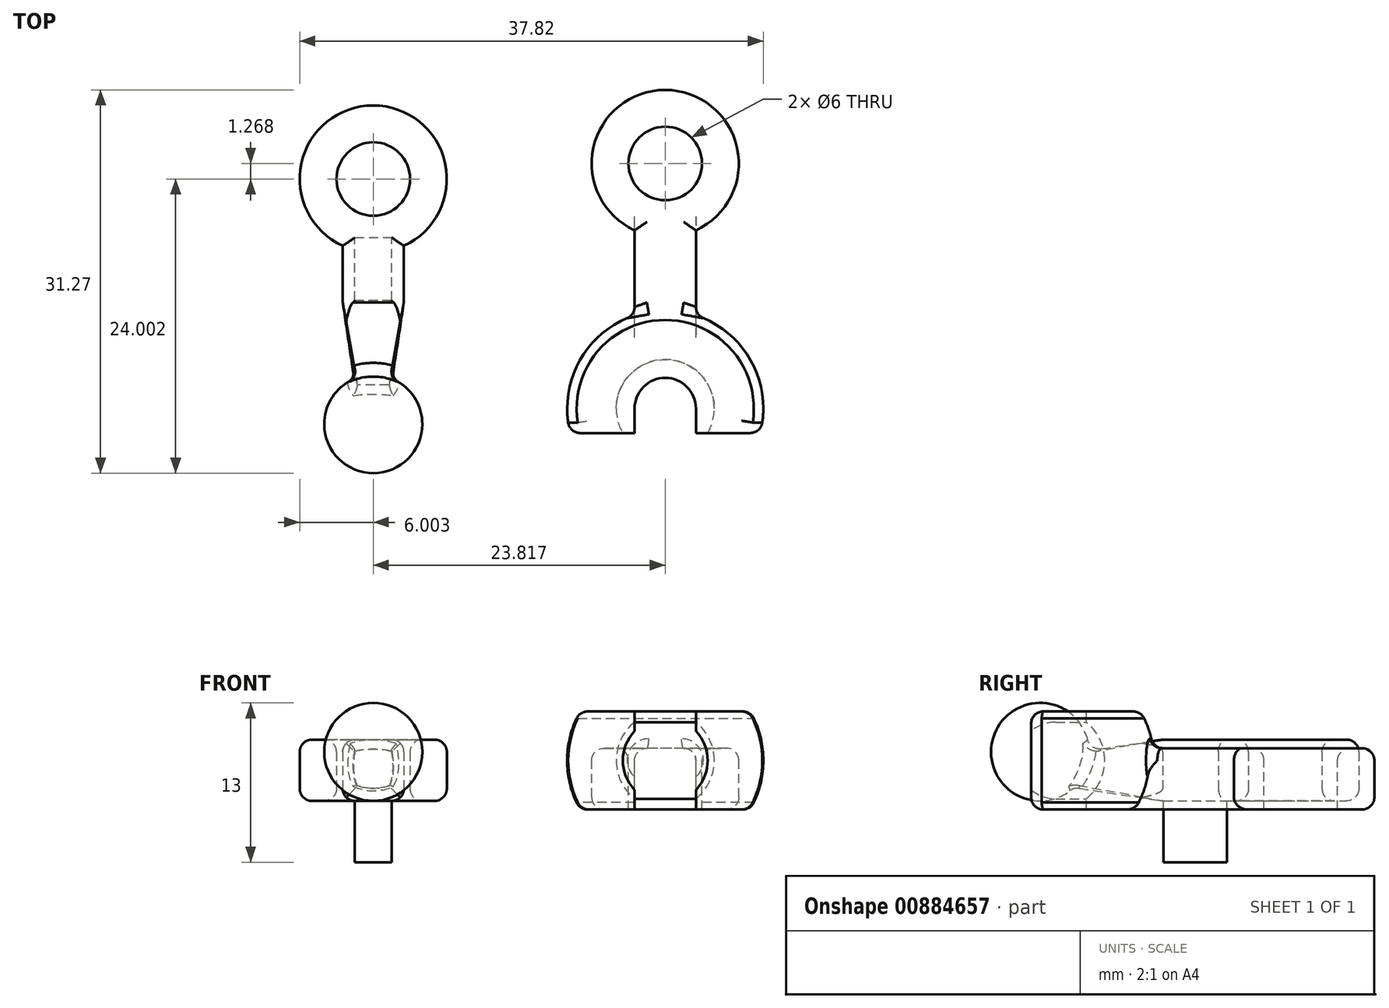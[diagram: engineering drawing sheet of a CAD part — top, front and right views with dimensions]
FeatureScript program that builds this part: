
annotation { "Feature Type Name" : "Feature", "Feature Type Description" : "" }
export const myFeature = defineFeature(function(context is Context, id is Id, definition is map)
    precondition{}
    {
        {
            var Q0;
            Q0=qCreatedBy(makeId("Front.planeOp"),FACE);
            var sketch = newSketch(context, id + "F0", { "sketchPlane" : qUnion([Q0])});
            skLineSegment(sketch, "E0.bottom", {"start": v(0, 0) * mm, "end": v(5, 0) * mm});
            skLineSegment(sketch, "E0.top", {"start": v(0, -5) * mm, "end": v(5, -5) * mm});
            skLineSegment(sketch, "E0.left", {"start": v(0, 0) * mm, "end": v(0, -5) * mm});
            skLineSegment(sketch, "E0.right", {"start": v(5, 0) * mm, "end": v(5, -5) * mm});
            skSolve(sketch);
        }
        {
            var Q0;
            Q0=makeQuery(id+"F0.imprint","IMPRINT",FACE,{"disambiguationData":[TD([[makeQuery(id+"F0.imprint","IMPRINT",EDGE,{"derivedFrom":sQuery(id+"F0.wireOp",EDGE,"E0.bottom")}),-1.0]])]});
            extrude(context, id + "F1", {"entities" : qUnion([Q0]), "depth" : 20 * mm, "offsetDistance" : 25 * mm});
        }
        {
            var Q0;
            Q0=makeQuery(id+"F1.opExtrude","CAP_FACE",FACE,{"disambiguationData":[OSD([sQuery(id+"F0.wireOp",EDGE,"E0.bottom"),sQuery(id+"F0.wireOp",EDGE,"E0.top"),sQuery(id+"F0.wireOp",EDGE,"E0.left"),sQuery(id+"F0.wireOp",EDGE,"E0.right")])],"isStart":false});
            var sketch = newSketch(context, id + "F2", { "sketchPlane" : qUnion([Q0])});
            skLineSegment(sketch, "E1", {"start": v(2.5, -1) * mm, "end": v(2.5, -9) * mm, "construction": true});
            skLineSegment(sketch, "E2.0", {"start": v(0, 0) * mm, "end": v(2.5, 0) * mm});
            skLineSegment(sketch, "E3", {"start": v(2.5, 0) * mm, "end": v(5, 0) * mm});
            skLineSegment(sketch, "E4", {"start": v(-5.5, -1) * mm, "end": v(-5.5, -1) * mm});
            skLineSegment(sketch, "E5", {"start": v(-5.5, -1) * mm, "end": v(10.5, -1) * mm});
            skArc(sketch, "E6", {"start": v(10.5, -1) * mm, "mid": v(2.5, 7) * mm, "end": v(-5.5, -1) * mm});
            skArc(sketch, "E7", {"start": v(-5.5, -1) * mm, "mid": v(2.5, -9) * mm, "end": v(10.5, -1) * mm, "construction": true});
            skSolve(sketch);
        }
        {
            var Q0;
            {var subQ7=sQuery(id+"F2.wireOp",EDGE,"E2.0");Q0=makeQuery(id+"F2.imprint","IMPRINT",FACE,{"disambiguationData":[TD([[makeQuery(id+"F2.imprint","IMPRINT",EDGE,{"derivedFrom":subQ7}),1.0]])]});}
            var Q1;
            Q1=sQuery(id+"F2.wireOp",EDGE,"E5");
            revolve(context, id + "F3", {"operationType" : NewBodyOperationType.ADD, "surfaceOperationType" : NewSurfaceOperationType.NEW, "entities" : qUnion([Q0]), "axis" : qUnion([Q1]), "revolveType" : RevolveType.FULL});
        }
        {
            var Q0;
            Q0=makeQuery(id+"F1.opExtrude","SWEPT_FACE",FACE,{"disambiguationData":[OSD([sQuery(id+"F0.wireOp",EDGE,"E0.bottom")])]});
            cPlane(context, id + "F4", {"entities" : qUnion([Q0]), "cplaneType" : CPlaneType.OFFSET, "offset" : 7 * mm, "width" : 150 * mm, "height" : 150 * mm});
        }
        {
            var Q0;
            Q0=makeQuery(id+"F1.opExtrude","SWEPT_FACE",FACE,{"disambiguationData":[OSD([sQuery(id+"F0.wireOp",EDGE,"E0.top")])]});
            cPlane(context, id + "F5", {"entities" : qUnion([Q0]), "cplaneType" : CPlaneType.OFFSET, "offset" : 4 * mm, "width" : 150 * mm, "height" : 150 * mm});
        }
        {
            var Q0;
            Q0=makeQuery(id+"F1.opExtrude","CAP_FACE",FACE,{"disambiguationData":[OSD([sQuery(id+"F0.wireOp",EDGE,"E0.bottom"),sQuery(id+"F0.wireOp",EDGE,"E0.top"),sQuery(id+"F0.wireOp",EDGE,"E0.left"),sQuery(id+"F0.wireOp",EDGE,"E0.right")])],"isStart":true});
            cPlane(context, id + "F6", {"entities" : qUnion([Q0]), "cplaneType" : CPlaneType.OFFSET, "offset" : 28 * mm, "oppositeDirection" : true, "width" : 150 * mm, "height" : 150 * mm});
        }
        {
            var Q0;
            Q0=qCreatedBy(id+"F4.planeOp",FACE);
            var sketch = newSketch(context, id + "F7", { "sketchPlane" : qUnion([Q0])});
            skLineSegment(sketch, "E8.bottom", {"start": v(-14.83, -1.3) * mm, "end": v(22.96, -1.3) * mm});
            skLineSegment(sketch, "E8.top", {"start": v(-14.83, -38.22) * mm, "end": v(22.96, -38.22) * mm});
            skLineSegment(sketch, "E8.left", {"start": v(-14.83, -1.3) * mm, "end": v(-14.83, -38.22) * mm});
            skLineSegment(sketch, "E8.right", {"start": v(22.96, -1.3) * mm, "end": v(22.96, -38.22) * mm});
            skSolve(sketch);
        }
        {
            var Q0;
            Q0=qCreatedBy(id+"F5.planeOp",FACE);
            var sketch = newSketch(context, id + "F8", { "sketchPlane" : qUnion([Q0])});
            skLineSegment(sketch, "E9.bottom", {"start": v(-20.63, 41.64) * mm, "end": v(25.17, 41.64) * mm});
            skLineSegment(sketch, "E9.top", {"start": v(-20.63, 7.79) * mm, "end": v(25.17, 7.79) * mm});
            skLineSegment(sketch, "E9.left", {"start": v(-20.63, 41.64) * mm, "end": v(-20.63, 7.79) * mm});
            skLineSegment(sketch, "E9.right", {"start": v(25.17, 41.64) * mm, "end": v(25.17, 7.79) * mm});
            skSolve(sketch);
        }
        {
            var Q0;
            Q0=qCreatedBy(id+"F6.planeOp",FACE);
            var sketch = newSketch(context, id + "F9", { "sketchPlane" : qUnion([Q0])});
            skLineSegment(sketch, "E10.bottom", {"start": v(14.18, 10.71) * mm, "end": v(-19.64, 10.71) * mm});
            skLineSegment(sketch, "E10.top", {"start": v(14.18, -15.2) * mm, "end": v(-19.64, -15.2) * mm});
            skLineSegment(sketch, "E10.left", {"start": v(14.18, 10.71) * mm, "end": v(14.18, -15.2) * mm});
            skLineSegment(sketch, "E10.right", {"start": v(-19.64, 10.71) * mm, "end": v(-19.64, -15.2) * mm});
            skSolve(sketch);
        }
        {
            var Q0;
            Q0 = qSketchRegion(id + "F9", true);
            extrude(context, id + "F10", {"entities" : qUnion([Q0]), "operationType" : NewBodyOperationType.REMOVE, "depth" : 6 * mm, "offsetDistance" : 25 * mm});
        }
        {
            var Q0;
            {var subQ5=makeQuery(id+"F1.opExtrude","CAP_EDGE",EDGE,{"disambiguationData":[OSD([sQuery(id+"F0.wireOp",EDGE,"E0.top")])],"isStart":false});Q0=makeQuery(id+"F2.imprint","IMPRINT",FACE,{"disambiguationData":[TD([[makeQuery(id+"F2.imprint","IMPRINT",EDGE,{"derivedFrom":subQ5}),1.0]])]});}
            var sketch = newSketch(context, id + "F11", { "sketchPlane" : qUnion([Q0])});
            skLineSegment(sketch, "E11.0", {"start": v(-5.5, -1) * mm, "end": v(-1.5, -1) * mm, "construction": true});
            skLineSegment(sketch, "E11.1", {"start": v(2.5, -1) * mm, "end": v(2.5, -9) * mm, "construction": true});
            skArc(sketch, "E12", {"start": v(-1.5, -1) * mm, "mid": v(2.5, -5) * mm, "end": v(6.5, -1) * mm, "construction": true});
            skArc(sketch, "E13", {"start": v(6.5, -1) * mm, "mid": v(2.5, 3) * mm, "end": v(-1.5, -1) * mm});
            skLineSegment(sketch, "E14", {"start": v(-1.5, -1) * mm, "end": v(6.5, -1) * mm});
            skLineSegment(sketch, "E15", {"start": v(6.5, -1) * mm, "end": v(10.5, -1) * mm, "construction": true});
            skSolve(sketch);
        }
        {
            var Q0;
            Q0 = qSketchRegion(id + "F11", true);
            var Q1;
            Q1=sQuery(id+"F11.wireOp",EDGE,"E14");
            revolve(context, id + "F12", {"operationType" : NewBodyOperationType.REMOVE, "surfaceOperationType" : NewSurfaceOperationType.NEW, "entities" : qUnion([Q0]), "axis" : qUnion([Q1]), "revolveType" : RevolveType.FULL, "oppositeDirection" : true});
        }
        {
            var Q0;
            Q0=makeQuery(id+"F10.boolean.opBoolean","COPY",FACE,{"derivedFrom":makeQuery(id+"F10.opExtrude","CAP_FACE",FACE,{"disambiguationData":[OSD([sQuery(id+"F9.wireOp",EDGE,"E10.bottom"),sQuery(id+"F9.wireOp",EDGE,"E10.top"),sQuery(id+"F9.wireOp",EDGE,"E10.left"),sQuery(id+"F9.wireOp",EDGE,"E10.right")])],"isStart":false})});
            var sketch = newSketch(context, id + "F13", { "sketchPlane" : qUnion([Q0])});
            skLineSegment(sketch, "E16.0", {"start": v(2.5, -1) * mm, "end": v(2.5, -9) * mm});
            skLineSegment(sketch, "E17.bottom", {"start": v(0, 11.1) * mm, "end": v(5, 11.1) * mm});
            skLineSegment(sketch, "E17.top", {"start": v(0, -15.2) * mm, "end": v(5, -15.2) * mm});
            skLineSegment(sketch, "E17.left", {"start": v(0, 11.1) * mm, "end": v(0, -15.2) * mm});
            skLineSegment(sketch, "E17.right", {"start": v(5, 11.1) * mm, "end": v(5, -15.2) * mm});
            skSolve(sketch);
        }
        {
            var Q0;
            Q0 = qSketchRegion(id + "F13", true);
            extrude(context, id + "F14", {"entities" : qUnion([Q0]), "operationType" : NewBodyOperationType.REMOVE, "oppositeDirection" : true, "depth" : 2 * mm, "offsetDistance" : 25 * mm});
        }
        {
            var Q0;
            Q0=qCreatedBy(id+"F4.planeOp",FACE);
            var sketch = newSketch(context, id + "F15", { "sketchPlane" : qUnion([Q0])});
            skCircle(sketch, "E18", {"center": v(2.5, -20) * mm, "radius": 2.5 * mm});
            skSolve(sketch);
        }
        {
            var Q0;
            Q0=makeQuery(id+"F15.imprint","IMPRINT",FACE,{"disambiguationData":[TD([[makeQuery(id+"F15.imprint","IMPRINT",EDGE,{"derivedFrom":sQuery(id+"F15.wireOp",EDGE,"E18")}),1.0]])]});
            extrude(context, id + "F16", {"entities" : qUnion([Q0]), "operationType" : NewBodyOperationType.REMOVE, "oppositeDirection" : true, "depth" : 25 * mm, "offsetDistance" : 25 * mm});
        }
        {
            var Q0;
            Q0 = qSketchRegion(id + "F7", true);
            extrude(context, id + "F17", {"entities" : qUnion([Q0]), "operationType" : NewBodyOperationType.REMOVE, "oppositeDirection" : true, "depth" : 4 * mm, "offsetDistance" : 25 * mm});
        }
        {
            var Q0;
            Q0 = qSketchRegion(id + "F8", true);
            extrude(context, id + "F18", {"entities" : qUnion([Q0]), "operationType" : NewBodyOperationType.REMOVE, "oppositeDirection" : true, "depth" : 4 * mm, "offsetDistance" : 25 * mm});
        }
        {
            var Q0;
            Q0=makeQuery(id+"F1.opExtrude","SWEPT_FACE",FACE,{"disambiguationData":[OSD([sQuery(id+"F0.wireOp",EDGE,"E0.bottom")])]});
            var sketch = newSketch(context, id + "F19", { "sketchPlane" : qUnion([Q0])});
            skCircle(sketch, "E19", {"center": v(2.5, 0) * mm, "radius": 6 * mm});
            skCircle(sketch, "E20", {"center": v(2.5, 0) * mm, "radius": 3 * mm});
            skSolve(sketch);
        }
        {
            var Q0;
            {var subQ1=sQuery(id+"F0.wireOp",EDGE,"E0.bottom");var subQ6=makeQuery(id+"F1.opExtrude","CAP_EDGE",EDGE,{"disambiguationData":[OSD([subQ1])],"isStart":true});Q0=makeQuery(id+"F19.imprint","IMPRINT",FACE,{"disambiguationData":[TD([[makeQuery(id+"F19.imprint","IMPRINT",EDGE,{"derivedFrom":subQ6}),-1.0]])]});}
            var Q1;
            {var subQ1=sQuery(id+"F0.wireOp",EDGE,"E0.bottom");var subQ6=makeQuery(id+"F1.opExtrude","CAP_EDGE",EDGE,{"disambiguationData":[OSD([subQ1])],"isStart":true});Q1=makeQuery(id+"F19.imprint","IMPRINT",FACE,{"disambiguationData":[TD([[makeQuery(id+"F19.imprint","IMPRINT",EDGE,{"derivedFrom":subQ6}),1.0]])]});}
            extrude(context, id + "F20", {"entities" : qUnion([Q0, Q1]), "operationType" : NewBodyOperationType.REMOVE, "oppositeDirection" : true, "depth" : 25 * mm, "offsetDistance" : 25 * mm});
        }
        {
            var Q0;
            {var subQ0=sQuery(id+"F19.wireOp",EDGE,"E19");var subQ1=sQuery(id+"F0.wireOp",EDGE,"E0.bottom");var subQ2=makeQuery(id+"F1.opExtrude","SWEPT_EDGE",EDGE,{"disambiguationData":[OSD([subQ1,sQuery(id+"F0.wireOp",EDGE,"E0.left")])]});var subQ3=makeQuery(id+"F19.imprint","INTERSECT",VERTEX,{"derivedFrom":[subQ2,subQ0]});Q0=makeQuery(id+"F19.imprint","IMPRINT",FACE,{"disambiguationData":[TD([[makeQuery(id+"F19.imprint","IMPRINT",EDGE,{"disambiguationData":[TD([[subQ3,1.0]])],"derivedFrom":subQ0}),1.0]])]});}
            extrude(context, id + "F21", {"entities" : qUnion([Q0]), "operationType" : NewBodyOperationType.ADD, "oppositeDirection" : true, "depth" : 5 * mm, "offsetDistance" : 25 * mm});
        }
        {
            var Q0;
            Q0=makeQuery(id+"F17.boolean.opBoolean","INTERSECT",EDGE,{"derivedFrom":[makeQuery(id+"F3.opRevolve","SWEPT_FACE",FACE,{"disambiguationData":[OSD([sQuery(id+"F2.wireOp",EDGE,"E6")])]}),makeQuery(id+"F17.opExtrude","CAP_FACE",FACE,{"disambiguationData":[OSD([sQuery(id+"F7.wireOp",EDGE,"E8.bottom"),sQuery(id+"F7.wireOp",EDGE,"E8.top"),sQuery(id+"F7.wireOp",EDGE,"E8.left"),sQuery(id+"F7.wireOp",EDGE,"E8.right")])],"isStart":false})]});
            var Q1;
            Q1=makeQuery(id+"F18.boolean.opBoolean","INTERSECT",EDGE,{"disambiguationData":[OD(1.0)],"derivedFrom":[makeQuery(id+"F3.opRevolve","SWEPT_FACE",FACE,{"disambiguationData":[OSD([sQuery(id+"F2.wireOp",EDGE,"E6")])]}),makeQuery(id+"F18.opExtrude","CAP_FACE",FACE,{"disambiguationData":[OSD([sQuery(id+"F8.wireOp",EDGE,"E9.bottom"),sQuery(id+"F8.wireOp",EDGE,"E9.top"),sQuery(id+"F8.wireOp",EDGE,"E9.left"),sQuery(id+"F8.wireOp",EDGE,"E9.right")])],"isStart":false})]});
            var Q2;
            Q2=makeQuery(id+"F18.boolean.opBoolean","INTERSECT",EDGE,{"disambiguationData":[OD(0.0)],"derivedFrom":[makeQuery(id+"F3.opRevolve","SWEPT_FACE",FACE,{"disambiguationData":[OSD([sQuery(id+"F2.wireOp",EDGE,"E6")])]}),makeQuery(id+"F18.opExtrude","CAP_FACE",FACE,{"disambiguationData":[OSD([sQuery(id+"F8.wireOp",EDGE,"E9.bottom"),sQuery(id+"F8.wireOp",EDGE,"E9.top"),sQuery(id+"F8.wireOp",EDGE,"E9.left"),sQuery(id+"F8.wireOp",EDGE,"E9.right")])],"isStart":false})]});
            var Q3;
            {var subQ0=sQuery(id+"F19.wireOp",EDGE,"E20");Q3=makeQuery(id+"F21.boolean.opBoolean","MERGE",EDGE,{"derivedFrom":[makeQuery(id+"F20.boolean.opBoolean","COPY",EDGE,{"derivedFrom":makeQuery(id+"F20.opExtrude","CAP_EDGE",EDGE,{"disambiguationData":[OSD([subQ0])],"isStart":true})}),makeQuery(id+"F21.opExtrude","CAP_EDGE",EDGE,{"disambiguationData":[OSD([subQ0])],"isStart":true})]});}
            var Q4;
            {var subQ0=sQuery(id+"F0.wireOp",EDGE,"E0.bottom");Q4=makeQuery(id+"F21.boolean.opBoolean","MERGE",FACE,{"derivedFrom":[makeQuery(id+"F1.opExtrude","SWEPT_FACE",FACE,{"disambiguationData":[OSD([subQ0])]}),makeQuery(id+"F21.opExtrude","CAP_FACE",FACE,{"disambiguationData":[OSD([subQ0,sQuery(id+"F0.wireOp",EDGE,"E0.left"),sQuery(id+"F0.wireOp",EDGE,"E0.right"),sQuery(id+"F19.wireOp",EDGE,"E19"),sQuery(id+"F19.wireOp",EDGE,"E20")])],"isStart":true})]});}
            var Q5;
            Q5=makeQuery(id+"F21.opExtrude","CAP_EDGE",EDGE,{"disambiguationData":[OSD([sQuery(id+"F19.wireOp",EDGE,"E19")])],"isStart":false});
            fillet(context, id + "F22", {"entities" : qUnion([Q0, Q1, Q2, Q3, Q4, Q5]), "radius" : 1 * mm, "tangentPropagation" : true, "allowEdgeOverflow" : false});
        }
        {
            var Q0;
            {var subQ0=makeQuery(id+"F3.opRevolve","SWEPT_FACE",FACE,{"disambiguationData":[OSD([sQuery(id+"F2.wireOp",EDGE,"E6")])]});var subQ1=makeQuery(id+"F10.opExtrude","CAP_FACE",FACE,{"disambiguationData":[OSD([sQuery(id+"F9.wireOp",EDGE,"E10.bottom"),sQuery(id+"F9.wireOp",EDGE,"E10.top"),sQuery(id+"F9.wireOp",EDGE,"E10.left"),sQuery(id+"F9.wireOp",EDGE,"E10.right")])],"isStart":false});Q0=makeQuery(id+"F14.boolean.opBoolean","SPLIT",EDGE,{"disambiguationData":[TD([makeQuery(id+"F14.opExtrude","SWEPT_FACE",FACE,{"disambiguationData":[OSD([sQuery(id+"F13.wireOp",EDGE,"E17.right")])]})])],"derivedFrom":makeQuery(id+"F10.boolean.opBoolean","INTERSECT",EDGE,{"derivedFrom":[subQ0,subQ1]})});}
            var Q1;
            {var subQ0=makeQuery(id+"F3.opRevolve","SWEPT_FACE",FACE,{"disambiguationData":[OSD([sQuery(id+"F2.wireOp",EDGE,"E6")])]});var subQ1=makeQuery(id+"F10.opExtrude","CAP_FACE",FACE,{"disambiguationData":[OSD([sQuery(id+"F9.wireOp",EDGE,"E10.bottom"),sQuery(id+"F9.wireOp",EDGE,"E10.top"),sQuery(id+"F9.wireOp",EDGE,"E10.left"),sQuery(id+"F9.wireOp",EDGE,"E10.right")])],"isStart":false});Q1=makeQuery(id+"F14.boolean.opBoolean","SPLIT",EDGE,{"disambiguationData":[TD([makeQuery(id+"F14.opExtrude","SWEPT_FACE",FACE,{"disambiguationData":[OSD([sQuery(id+"F13.wireOp",EDGE,"E17.left")])]})])],"derivedFrom":makeQuery(id+"F10.boolean.opBoolean","INTERSECT",EDGE,{"derivedFrom":[subQ0,subQ1]})});}
            fillet(context, id + "F23", {"entities" : qUnion([Q0, Q1]), "radius" : 1 * mm, "tangentPropagation" : true, "allowEdgeOverflow" : false});
        }
        {
            var Q0;
            Q0=qCreatedBy(makeId("Top.planeOp"),FACE);
            var sketch = newSketch(context, id + "F24", { "sketchPlane" : qUnion([Q0])});
            skLineSegment(sketch, "E21.bottom", {"start": v(-34.22, -35.67) * mm, "end": v(-39.22, -35.67) * mm});
            skLineSegment(sketch, "E21.top", {"start": v(-34.22, -25.67) * mm, "end": v(-39.22, -25.67) * mm});
            skLineSegment(sketch, "E21.left", {"start": v(-34.22, -35.67) * mm, "end": v(-34.22, -25.67) * mm});
            skLineSegment(sketch, "E21.right", {"start": v(-39.22, -35.67) * mm, "end": v(-39.22, -25.67) * mm});
            skCircle(sketch, "E22", {"center": v(-36.72, -25.67) * mm, "radius": 6 * mm});
            skCircle(sketch, "E23", {"center": v(-36.72, -25.67) * mm, "radius": 3 * mm});
            skSolve(sketch);
        }
        {
            var Q0;
            Q0 = qSketchRegion(id + "F24", true);
            extrude(context, id + "F25", {"entities" : qUnion([Q0]), "depth" : 5 * mm, "offsetDistance" : 25 * mm});
        }
        {
            var Q0;
            Q0=makeQuery(id+"F25.opExtrude","SWEPT_FACE",FACE,{"disambiguationData":[OSD([sQuery(id+"F24.wireOp",EDGE,"E21.bottom")])]});
            cPlane(context, id + "F26", {"entities" : qUnion([Q0]), "cplaneType" : CPlaneType.OFFSET, "offset" : 10 * mm, "width" : 150 * mm, "height" : 150 * mm});
        }
        {
            var Q0;
            Q0=qCreatedBy(id+"F26.planeOp",FACE);
            var sketch = newSketch(context, id + "F27", { "sketchPlane" : qUnion([Q0])});
            skPoint(sketch, "E24.0", {"position": v(-36.72, 5) * mm});
            skPoint(sketch, "E25.0", {"position": v(-36.72, 0) * mm});
            skPoint(sketch, "E26.0", {"position": v(-39.22, 2.5) * mm});
            skPoint(sketch, "E27.0", {"position": v(-34.22, 2.5) * mm});
            skLineSegment(sketch, "E28", {"start": v(-36.72, 5) * mm, "end": v(-36.72, 0) * mm, "construction": true});
            skLineSegment(sketch, "E29", {"start": v(-39.22, 2.5) * mm, "end": v(-34.22, 2.5) * mm, "construction": true});
            skPoint(sketch, "E30", {"position": v(-36.72, 2.5) * mm});
            skCircle(sketch, "E31", {"center": v(-36.72, 2.5) * mm, "radius": 1 * mm});
            skSolve(sketch);
        }
        {
            var Q1;
            Q1=makeQuery(id+"F25.opExtrude","SWEPT_FACE",FACE,{"disambiguationData":[OSD([sQuery(id+"F24.wireOp",EDGE,"E21.bottom")])]});
            var Q2;
            Q2=makeQuery(id+"F27.imprint","IMPRINT",FACE,{"disambiguationData":[TD([[makeQuery(id+"F27.imprint","IMPRINT",EDGE,{"derivedFrom":sQuery(id+"F27.wireOp",EDGE,"E31")}),1.0]])]});
            loft(context, id + "F28", {"operationType" : NewBodyOperationType.ADD, "sheetProfilesArray" : [{ "sheetProfileEntities" : qUnion([Q1]) }, { "sheetProfileEntities" : qUnion([Q2]) }]});
        }
        {
            var Q0;
            Q0=makeQuery(id+"F28.opLoft","CAP_FACE",FACE,{"disambiguationData":[OSD([makeQuery(id+"F27.imprint","IMPRINT",FACE,{"disambiguationData":[TD([[makeQuery(id+"F27.imprint","IMPRINT",EDGE,{"derivedFrom":sQuery(id+"F27.wireOp",EDGE,"E31")}),1.0]])]})])],"isStart":true});
            var sketch = newSketch(context, id + "F29", { "sketchPlane" : qUnion([Q0])});
            skFitSpline(sketch, "E32.0.0", {"points": [v(-36, 1.8) * mm, v(-35.92, 1.89) * mm, v(-35.84, 2) * mm, v(-35.8, 2.12) * mm, v(-35.74, 2.24) * mm, v(-35.72, 2.37) * mm, v(-35.72, 2.5) * mm, v(-35.72, 2.63) * mm, v(-35.74, 2.76) * mm, v(-35.8, 2.88) * mm, v(-35.84, 3) * mm, v(-35.92, 3.11) * mm, v(-36, 3.2) * mm], "construction": true});
            skFitSpline(sketch, "E32.0.1", {"points": [v(-36, 3.2) * mm, v(-36.1, 3.3) * mm, v(-36.21, 3.37) * mm, v(-36.33, 3.42) * mm, v(-36.46, 3.47) * mm, v(-36.58, 3.5) * mm, v(-36.72, 3.5) * mm, v(-36.85, 3.5) * mm, v(-36.98, 3.47) * mm, v(-37.1, 3.42) * mm, v(-37.22, 3.37) * mm, v(-37.33, 3.3) * mm, v(-37.42, 3.2) * mm], "construction": true});
            skFitSpline(sketch, "E32.0.2", {"points": [v(-37.42, 3.2) * mm, v(-37.52, 3.11) * mm, v(-37.59, 3) * mm, v(-37.64, 2.88) * mm, v(-37.7, 2.76) * mm, v(-37.72, 2.63) * mm, v(-37.72, 2.5) * mm, v(-37.72, 2.37) * mm, v(-37.7, 2.24) * mm, v(-37.64, 2.12) * mm, v(-37.6, 2) * mm, v(-37.52, 1.89) * mm, v(-37.42, 1.8) * mm], "construction": true});
            skFitSpline(sketch, "E32.0.3", {"points": [v(-37.42, 1.8) * mm, v(-37.33, 1.7) * mm, v(-37.22, 1.63) * mm, v(-37.1, 1.58) * mm, v(-36.98, 1.53) * mm, v(-36.85, 1.5) * mm, v(-36.72, 1.5) * mm, v(-36.58, 1.5) * mm, v(-36.46, 1.53) * mm, v(-36.33, 1.58) * mm, v(-36.21, 1.63) * mm, v(-36.1, 1.7) * mm, v(-36, 1.8) * mm], "construction": true});
            skPoint(sketch, "E33.0", {"position": v(-36.72, 2.5) * mm});
            skLineSegment(sketch, "E34", {"start": v(-36.72, 4) * mm, "end": v(-36.72, 0) * mm, "construction": true});
            skLineSegment(sketch, "E35.0", {"start": v(-34.22, 0) * mm, "end": v(-39.22, 0) * mm, "construction": true});
            skPoint(sketch, "E35.1", {"position": v(-36.72, 0) * mm});
            skLineSegment(sketch, "E36", {"start": v(-40.72, 4) * mm, "end": v(-32.72, 4) * mm});
            skArc(sketch, "E37", {"start": v(-40.72, 4) * mm, "mid": v(-36.72, 0) * mm, "end": v(-32.72, 4) * mm, "construction": true});
            skArc(sketch, "E38", {"start": v(-32.72, 4) * mm, "mid": v(-36.72, 8) * mm, "end": v(-40.72, 4) * mm});
            skSolve(sketch);
        }
        {
            var Q0;
            Q0=makeQuery(id+"F29.imprint","IMPRINT",FACE,{"disambiguationData":[TD([[makeQuery(id+"F29.imprint","IMPRINT",EDGE,{"derivedFrom":sQuery(id+"F29.wireOp",EDGE,"E36")}),1.0]])]});
            var Q1;
            Q1=sQuery(id+"F29.wireOp",EDGE,"E36");
            revolve(context, id + "F30", {"operationType" : NewBodyOperationType.ADD, "surfaceOperationType" : NewSurfaceOperationType.NEW, "entities" : qUnion([Q0]), "axis" : qUnion([Q1]), "revolveType" : RevolveType.FULL});
        }
        {
            var Q0;
            Q0=makeQuery(id+"F25.opExtrude","CAP_FACE",FACE,{"disambiguationData":[OSD([sQuery(id+"F24.wireOp",EDGE,"E21.bottom"),sQuery(id+"F24.wireOp",EDGE,"E21.left"),sQuery(id+"F24.wireOp",EDGE,"E21.right"),sQuery(id+"F24.wireOp",EDGE,"E22"),sQuery(id+"F24.wireOp",EDGE,"E23")])],"isStart":false});
            var Q1;
            Q1=makeQuery(id+"F25.opExtrude","CAP_FACE",FACE,{"disambiguationData":[OSD([sQuery(id+"F24.wireOp",EDGE,"E21.bottom"),sQuery(id+"F24.wireOp",EDGE,"E21.left"),sQuery(id+"F24.wireOp",EDGE,"E21.right"),sQuery(id+"F24.wireOp",EDGE,"E22"),sQuery(id+"F24.wireOp",EDGE,"E23")])],"isStart":true});
            fillet(context, id + "F31", {"entities" : qUnion([Q0, Q1]), "radius" : 1 * mm, "tangentPropagation" : true, "allowEdgeOverflow" : false});
        }
        {
            var Q0;
            {var subQ0=sQuery(id+"F27.wireOp",EDGE,"E31");var subQ1=sQuery(id+"F24.wireOp",EDGE,"E21.right");var subQ2=sQuery(id+"F24.wireOp",EDGE,"E21.bottom");var subQ3=sQuery(id+"F24.wireOp",EDGE,"E21.left");Q0=makeQuery(id+"F30.boolean.opBoolean","INTERSECT",EDGE,{"derivedFrom":[makeQuery(id+"F28.opLoft","SWEPT_FACE",FACE,{"disambiguationData":[OSD([subQ2,subQ3,subQ1,subQ0]),TDD([makeQuery(id+"F25.opExtrude","CAP_VERTEX",VERTEX,{"disambiguationData":[OSD([subQ2,subQ3])],"isStart":false}),makeQuery(id+"F25.opExtrude","CAP_VERTEX",VERTEX,{"disambiguationData":[OSD([subQ2,subQ1])],"isStart":true}),makeQuery(id+"F25.opExtrude","CAP_VERTEX",VERTEX,{"disambiguationData":[OSD([subQ2,subQ1])],"isStart":false}),makeQuery(id+"F25.opExtrude","SWEPT_EDGE",EDGE,{"disambiguationData":[OSD([subQ2,subQ1])]}),makeQuery(id+"F27.imprint","IMPRINT",EDGE,{"derivedFrom":subQ0})])]}),makeQuery(id+"F30.opRevolve","SWEPT_FACE",FACE,{"disambiguationData":[OSD([sQuery(id+"F29.wireOp",EDGE,"E38")])]})]});}
            var Q1;
            {var subQ0=sQuery(id+"F27.wireOp",EDGE,"E31");var subQ1=sQuery(id+"F24.wireOp",EDGE,"E21.bottom");var subQ2=sQuery(id+"F24.wireOp",EDGE,"E21.right");var subQ3=sQuery(id+"F24.wireOp",EDGE,"E21.left");Q1=makeQuery(id+"F30.boolean.opBoolean","INTERSECT",EDGE,{"derivedFrom":[makeQuery(id+"F28.opLoft","SWEPT_FACE",FACE,{"disambiguationData":[OSD([subQ1,subQ3,subQ2,subQ0]),TDD([makeQuery(id+"F25.opExtrude","CAP_VERTEX",VERTEX,{"disambiguationData":[OSD([subQ1,subQ3])],"isStart":true}),makeQuery(id+"F25.opExtrude","CAP_VERTEX",VERTEX,{"disambiguationData":[OSD([subQ1,subQ3])],"isStart":false}),makeQuery(id+"F25.opExtrude","CAP_VERTEX",VERTEX,{"disambiguationData":[OSD([subQ1,subQ2])],"isStart":false}),makeQuery(id+"F25.opExtrude","CAP_EDGE",EDGE,{"disambiguationData":[OSD([subQ1])],"isStart":false}),makeQuery(id+"F27.imprint","IMPRINT",EDGE,{"derivedFrom":subQ0})])]}),makeQuery(id+"F30.opRevolve","SWEPT_FACE",FACE,{"disambiguationData":[OSD([sQuery(id+"F29.wireOp",EDGE,"E38")])]})]});}
            var Q2;
            Q2=makeQuery(id+"F30.boolean.opBoolean","INTERSECT",EDGE,{"derivedFrom":[makeQuery(id+"F28.opLoft","SWEPT_FACE",FACE,{"disambiguationData":[OSD([sQuery(id+"F24.wireOp",EDGE,"E21.bottom"),sQuery(id+"F24.wireOp",EDGE,"E21.left"),sQuery(id+"F27.wireOp",EDGE,"E31")])]}),makeQuery(id+"F30.opRevolve","SWEPT_FACE",FACE,{"disambiguationData":[OSD([sQuery(id+"F29.wireOp",EDGE,"E38")])]})]});
            var Q3;
            {var subQ0=sQuery(id+"F27.wireOp",EDGE,"E31");var subQ1=sQuery(id+"F24.wireOp",EDGE,"E21.bottom");var subQ2=sQuery(id+"F24.wireOp",EDGE,"E21.right");var subQ3=sQuery(id+"F24.wireOp",EDGE,"E21.left");Q3=makeQuery(id+"F30.boolean.opBoolean","INTERSECT",EDGE,{"derivedFrom":[makeQuery(id+"F28.opLoft","SWEPT_FACE",FACE,{"disambiguationData":[OSD([subQ1,subQ3,subQ2,subQ0]),TDD([makeQuery(id+"F25.opExtrude","CAP_VERTEX",VERTEX,{"disambiguationData":[OSD([subQ1,subQ3])],"isStart":true}),makeQuery(id+"F25.opExtrude","CAP_VERTEX",VERTEX,{"disambiguationData":[OSD([subQ1,subQ2])],"isStart":true}),makeQuery(id+"F25.opExtrude","CAP_VERTEX",VERTEX,{"disambiguationData":[OSD([subQ1,subQ2])],"isStart":false}),makeQuery(id+"F25.opExtrude","CAP_EDGE",EDGE,{"disambiguationData":[OSD([subQ1])],"isStart":true}),makeQuery(id+"F27.imprint","IMPRINT",EDGE,{"derivedFrom":subQ0})])]}),makeQuery(id+"F30.opRevolve","SWEPT_FACE",FACE,{"disambiguationData":[OSD([sQuery(id+"F29.wireOp",EDGE,"E38")])]})]});}
            fillet(context, id + "F32", {"entities" : qUnion([Q0, Q1, Q2, Q3]), "radius" : 1 * mm, "tangentPropagation" : true, "allowEdgeOverflow" : false});
        }
        {
            var Q0;
            Q0=makeQuery(id+"F25.opExtrude","SWEPT_BODY",BODY,{"disambiguationData":[OSD([sQuery(id+"F24.wireOp",EDGE,"E21.bottom"),sQuery(id+"F24.wireOp",EDGE,"E21.left"),sQuery(id+"F24.wireOp",EDGE,"E21.right"),sQuery(id+"F24.wireOp",EDGE,"E22"),sQuery(id+"F24.wireOp",EDGE,"E23")])]});
            transform(context, id + "F33", {"entities" : qUnion([Q0]), "transformType" : TransformType.TRANSLATION_3D, "dx" : 15.4 * mm, "dy" : 24.4 * mm, "dz" : -4.3 * mm, "makeCopy" : false});
        }
        {
            var Q0;
            Q0=makeQuery(id+"F25.opExtrude","CAP_FACE",FACE,{"disambiguationData":[OSD([sQuery(id+"F24.wireOp",EDGE,"E21.bottom"),sQuery(id+"F24.wireOp",EDGE,"E21.left"),sQuery(id+"F24.wireOp",EDGE,"E21.right"),sQuery(id+"F24.wireOp",EDGE,"E22"),sQuery(id+"F24.wireOp",EDGE,"E23")])],"isStart":true});
            var sketch = newSketch(context, id + "F34", { "sketchPlane" : qUnion([Q0])});
            skLineSegment(sketch, "E39.bottom", {"start": v(-22.82, 11.19) * mm, "end": v(-19.82, 11.19) * mm});
            skLineSegment(sketch, "E39.top", {"start": v(-22.82, 6.04) * mm, "end": v(-19.82, 6.04) * mm});
            skLineSegment(sketch, "E39.left", {"start": v(-22.82, 11.19) * mm, "end": v(-22.82, 6.04) * mm});
            skLineSegment(sketch, "E39.right", {"start": v(-19.82, 11.19) * mm, "end": v(-19.82, 6.04) * mm});
            skSolve(sketch);
        }
        {
            var Q0;
            Q0=makeQuery(id+"F34.imprint","IMPRINT",FACE,{"disambiguationData":[TD([[makeQuery(id+"F34.imprint","IMPRINT",EDGE,{"derivedFrom":sQuery(id+"F34.wireOp",EDGE,"E39.bottom")}),-1.0]])]});
            extrude(context, id + "F35", {"entities" : qUnion([Q0]), "operationType" : NewBodyOperationType.ADD, "depth" : 5 * mm, "offsetDistance" : 25 * mm});
        }
    });
